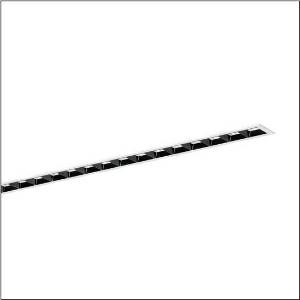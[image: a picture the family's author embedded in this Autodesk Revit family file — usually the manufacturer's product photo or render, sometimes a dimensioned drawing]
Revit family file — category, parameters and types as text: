
# Revit family: silica_r__21_51mx11db35wb_5c76
name_source: partatom
category: Lighting Fixtures
units: mm (PartAtom-declared; Revit-internal decimal feet)

## family parameters
Cut with Voids When Loaded = No
Host = Face
Light Source = No
Part Type = Normal
Room Calculation Point = No
Round Connector Dimension = Use Diameter
Shared = No

## types (1)
- --- (1 x LED, 5400 lm, 34.3 W, 3000K)
    Apparent Load = 34 VA
    CIE Flux Codes = 87 99 100 100 100
    Color Rendering = 80
    Color Temperature = 3000K
    Default Elevation = 1800 mm
    Description = Silica® 21, office luminaire, primary light control with darklight reflector, of PMMA, black, CAT 2 (L<= 3000cd/m²), light emission: direct distribution, primary light characteristic: symmetric, installation type: recessed, LED, rated luminous flux: 5.400lm, luminous efficacy: 157lm/W, light colour: 830, colour temperature: 3000K, control gear: DALI 2, with terminal, 3+2-pole, max. 2.5mm², mains connection: 220..240V, AC, 50/60Hz, rated input power: 34.3W, luminaire housing, of aluminium, traffic white (RAL 9016), length: 1.528mm, width: 79mm, height: 53mm, protection rating (complete): IP20, insulation class (complete): insulation class I (protective earthing), certification: CE, ENEC, VDE, permissible operating ambient temperature: 0..+35°C, standard: EN 50419, packaging unit: 1 piece
    Height = 0 mm  [stored 0 ft]
    Lamp = 1 x LED
    Lamp Light Flux = 5400 lm
    Lamp Power = 34.3 W
    Lamp count = 1
    Length = 1527 mm
    Luminous efficacy = 157 lm/W
    Manufacturer = Siteco
    ModVariant = No
    Model = 51MX11DB35WB
    Mounting Place = Ceiling
    Mounting Type = Recessed
    Number of Poles = 1
    OnlyDefault = Yes
    Power Factor = 1
    Product Name = Silica® 21
    Product group = office luminaire | ceiling recessed
    ProductGroupID = 401
    Protection Class = Protection class I
    Protection Degree = IP 20
    RLX_Detail_Level = 1
    RLX_Emergency_Light_Flux = 0 lm
    RLX_Emergency_Type = 0
    RLX_Emergency_Type_DB = No
    RlxData = <blob elided: 42189 chars, md5=fc19460c>
    Socket = socket
    Standby Power = 0 W
    System Light Flux = 5400 lm
    System Power = 34 W
    Type Comments = factory setting: luminous flux: 100 % | dim-lin: 254 | 393 mA
    Type Image = l_1335880.jpg
    URL = http://relux.com
    VarID = @adj_123412
    Voltage = 0 V
    Weight = 0.00 kg
    Width = 79 mm

note: [stored X ft] marks values corroborated as IEEE doubles in the binary element streams (Revit-internal decimal feet)

## geometry (parser evidence)
native form markers: Blend x4, Sweep x10
no freeform markers — native parametric forms only
